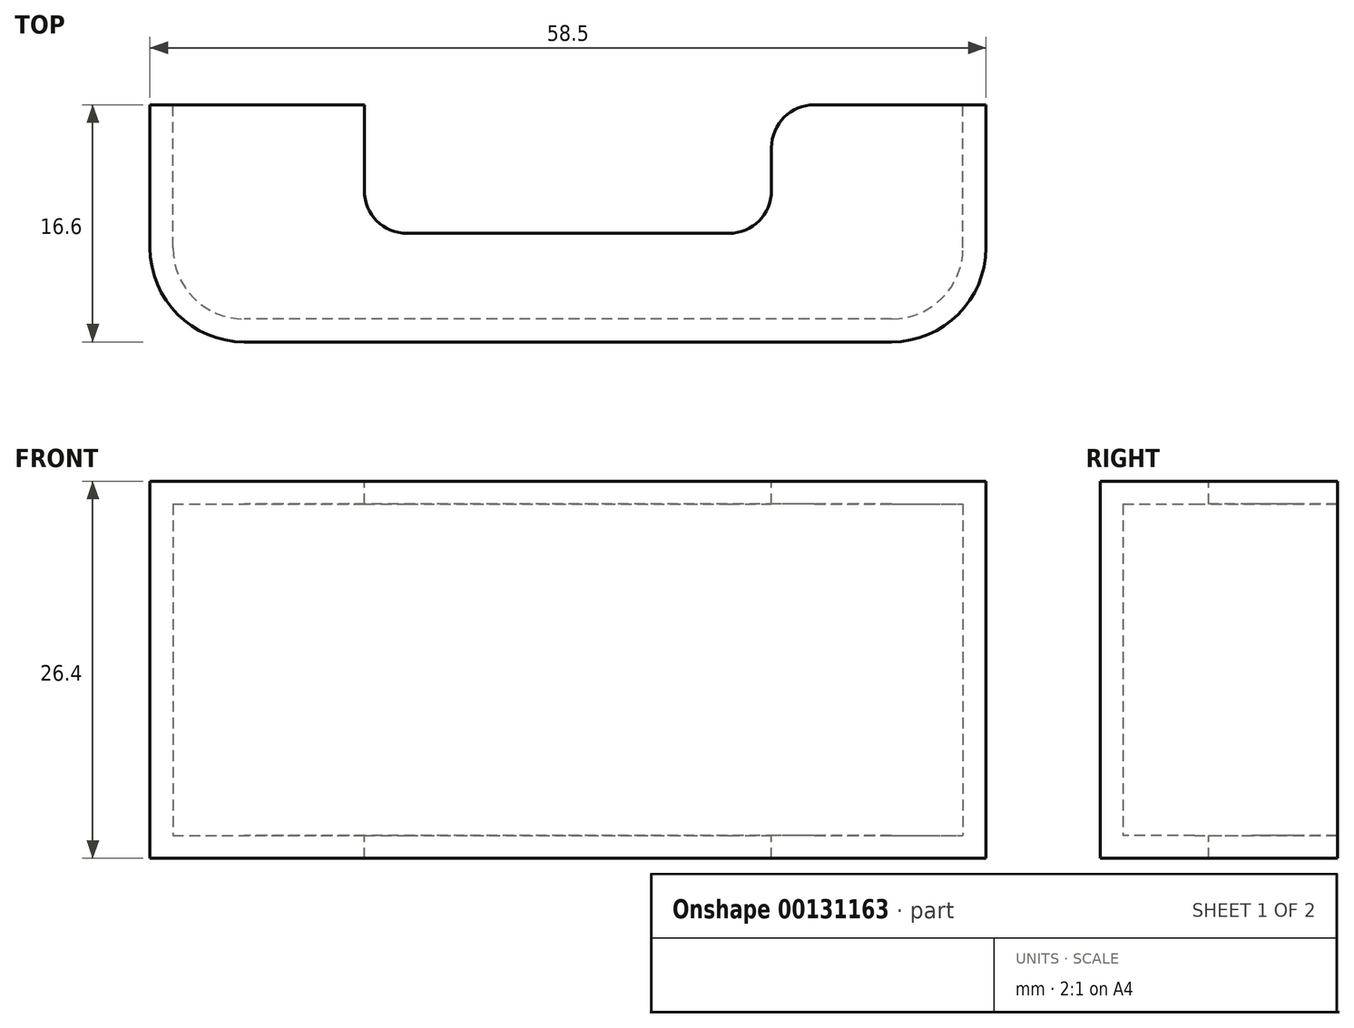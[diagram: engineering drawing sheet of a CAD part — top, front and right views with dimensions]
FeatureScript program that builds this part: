
annotation { "Feature Type Name" : "Feature", "Feature Type Description" : "" }
export const myFeature = defineFeature(function(context is Context, id is Id, definition is map)
    precondition{}
    {
        {
            var Q0;
            Q0=qCreatedBy(makeId("Top.planeOp"),FACE);
            var sketch = newSketch(context, id + "F0", { "sketchPlane" : qUnion([Q0])});
            skLineSegment(sketch, "E0.top", {"start": v(27.65, 7.5) * mm, "end": v(-27.65, 7.5) * mm});
            skPoint(sketch, "E0.middle", {"position": v(0, 0) * mm});
            skLineSegment(sketch, "E1.0", {"start": v(29.25, -9.1) * mm, "end": v(29.25, 7.5) * mm});
            skLineSegment(sketch, "E1.1", {"start": v(29.25, -9.1) * mm, "end": v(-29.25, -9.1) * mm});
            skLineSegment(sketch, "E1.2", {"start": v(-29.25, -9.1) * mm, "end": v(-29.25, 7.5) * mm});
            skPoint(sketch, "E0.bottom.end.orphan", {"position": v(-27.65, -7.5) * mm});
            skPoint(sketch, "E0.left.start.orphan", {"position": v(27.65, -7.5) * mm});
            skLineSegment(sketch, "E2", {"start": v(-29.25, 7.5) * mm, "end": v(-27.65, 7.5) * mm});
            skLineSegment(sketch, "E3", {"start": v(27.65, 7.5) * mm, "end": v(29.25, 7.5) * mm});
            skSolve(sketch);
        }
        {
            var Q0;
            Q0 = qSketchRegion(id + "F0", true);
            extrude(context, id + "F1", {"entities" : qUnion([Q0]), "depth" : 26.4 * mm});
        }
        {
            var Q0;
            Q0=makeQuery(id+"F1.opExtrude","SWEPT_EDGE",EDGE,{"disambiguationData":[OSD([sQuery(id+"F0.wireOp",EDGE,"E1.0"),sQuery(id+"F0.wireOp",EDGE,"E1.1")])]});
            var Q1;
            Q1=makeQuery(id+"F1.opExtrude","SWEPT_EDGE",EDGE,{"disambiguationData":[OSD([sQuery(id+"F0.wireOp",EDGE,"E1.1"),sQuery(id+"F0.wireOp",EDGE,"E1.2")])]});
            fillet(context, id + "F2", {"entities" : qUnion([Q0, Q1]), "radius" : 6.6 * mm, "tangentPropagation" : true, "allowEdgeOverflow" : false});
        }
        {
            var Q0;
            Q0=makeQuery(id+"F1.opExtrude","SWEPT_FACE",FACE,{"disambiguationData":[OSD([sQuery(id+"F0.wireOp",EDGE,"E0.top"),sQuery(id+"F0.wireOp",EDGE,"E2"),sQuery(id+"F0.wireOp",EDGE,"E3")])]});
            shell(context, id + "F3", {"entities" : qUnion([Q0]), "thickness" : 1.6 * mm});
        }
        {
            var Q0;
            Q0=makeQuery(id+"F1.opExtrude","CAP_FACE",FACE,{"disambiguationData":[OSD([sQuery(id+"F0.wireOp",EDGE,"E0.top"),sQuery(id+"F0.wireOp",EDGE,"E1.0"),sQuery(id+"F0.wireOp",EDGE,"E1.1"),sQuery(id+"F0.wireOp",EDGE,"E1.2"),sQuery(id+"F0.wireOp",EDGE,"E2"),sQuery(id+"F0.wireOp",EDGE,"E3")])],"isStart":false});
            var sketch = newSketch(context, id + "F4", { "sketchPlane" : qUnion([Q0])});
            skLineSegment(sketch, "E4", {"start": v(-14.25, 7.5) * mm, "end": v(-14.25, -60.34) * mm, "construction": true});
            skLineSegment(sketch, "E5", {"start": v(14.25, 7.5) * mm, "end": v(14.25, -22.1) * mm, "construction": true});
            skLineSegment(sketch, "E6", {"start": v(-31.93, -1.5) * mm, "end": v(33.13, -1.5) * mm, "construction": true});
            skLineSegment(sketch, "E7.bottom", {"start": v(-14.25, 7.5) * mm, "end": v(14.25, 7.5) * mm});
            skLineSegment(sketch, "E7.top", {"start": v(-14.25, -1.5) * mm, "end": v(14.25, -1.5) * mm});
            skLineSegment(sketch, "E7.left", {"start": v(-14.25, 7.5) * mm, "end": v(-14.25, -1.5) * mm});
            skLineSegment(sketch, "E7.right", {"start": v(14.25, 7.5) * mm, "end": v(14.25, -1.5) * mm});
            skSolve(sketch);
        }
        {
            var Q0;
            Q0=makeQuery(id+"F4.imprint","IMPRINT",FACE,{"disambiguationData":[TD([[makeQuery(id+"F4.imprint","IMPRINT",EDGE,{"derivedFrom":sQuery(id+"F4.wireOp",EDGE,"E7.bottom")}),-1.0]])]});
            extrude(context, id + "F5", {"entities" : qUnion([Q0]), "operationType" : NewBodyOperationType.REMOVE, "endBound" : BoundingType.THROUGH_ALL, "oppositeDirection" : true, "depth" : 25 * mm});
        }
        {
            var Q0;
            {var subQ0=sQuery(id+"F0.wireOp",EDGE,"E3");var subQ1=sQuery(id+"F0.wireOp",EDGE,"E2");var subQ2=sQuery(id+"F0.wireOp",EDGE,"E1.2");var subQ3=sQuery(id+"F0.wireOp",EDGE,"E1.1");var subQ4=sQuery(id+"F0.wireOp",EDGE,"E1.0");var subQ5=sQuery(id+"F0.wireOp",EDGE,"E0.top");var subQ6=makeQuery(id+"F1.opExtrude","CAP_FACE",FACE,{"disambiguationData":[OSD([subQ5,subQ4,subQ3,subQ2,subQ1,subQ0])],"isStart":false});var subQ7=sQuery(id+"F4.wireOp",EDGE,"E7.top");var subQ8=sQuery(id+"F4.wireOp",EDGE,"E7.right");Q0=makeQuery(id+"F5.boolean.opBoolean","COPY",EDGE,{"disambiguationData":[TD([subQ6])],"derivedFrom":makeQuery(id+"F5.opExtrude","SWEPT_EDGE",EDGE,{"disambiguationData":[OSD([subQ7,subQ8])]})});}
            var Q1;
            {var subQ0=sQuery(id+"F0.wireOp",EDGE,"E3");var subQ1=sQuery(id+"F0.wireOp",EDGE,"E2");var subQ2=sQuery(id+"F0.wireOp",EDGE,"E1.2");var subQ3=sQuery(id+"F0.wireOp",EDGE,"E1.1");var subQ4=sQuery(id+"F0.wireOp",EDGE,"E1.0");var subQ5=sQuery(id+"F0.wireOp",EDGE,"E0.top");var subQ6=makeQuery(id+"F1.opExtrude","CAP_FACE",FACE,{"disambiguationData":[OSD([subQ5,subQ4,subQ3,subQ2,subQ1,subQ0])],"isStart":false});var subQ7=sQuery(id+"F4.wireOp",EDGE,"E7.right");Q1=makeQuery(id+"F5.boolean.opBoolean","COPY",EDGE,{"disambiguationData":[TD([subQ6])],"derivedFrom":makeQuery(id+"F5.opExtrude","SWEPT_EDGE",EDGE,{"disambiguationData":[OSD([subQ5,subQ1,subQ0,sQuery(id+"F4.wireOp",EDGE,"E7.bottom"),subQ7])]})});}
            var Q2;
            {var subQ0=sQuery(id+"F0.wireOp",EDGE,"E3");var subQ1=sQuery(id+"F0.wireOp",EDGE,"E2");var subQ2=sQuery(id+"F0.wireOp",EDGE,"E1.2");var subQ3=sQuery(id+"F0.wireOp",EDGE,"E1.1");var subQ4=sQuery(id+"F0.wireOp",EDGE,"E1.0");var subQ5=sQuery(id+"F0.wireOp",EDGE,"E0.top");var subQ6=makeQuery(id+"F1.opExtrude","CAP_FACE",FACE,{"disambiguationData":[OSD([subQ5,subQ4,subQ3,subQ2,subQ1,subQ0])],"isStart":true});var subQ7=sQuery(id+"F4.wireOp",EDGE,"E7.right");Q2=makeQuery(id+"F5.boolean.opBoolean","COPY",EDGE,{"disambiguationData":[TD([subQ6])],"derivedFrom":makeQuery(id+"F5.opExtrude","SWEPT_EDGE",EDGE,{"disambiguationData":[OSD([subQ5,subQ1,subQ0,sQuery(id+"F4.wireOp",EDGE,"E7.bottom"),subQ7])]})});}
            var Q3;
            {var subQ0=sQuery(id+"F0.wireOp",EDGE,"E3");var subQ1=sQuery(id+"F0.wireOp",EDGE,"E2");var subQ2=sQuery(id+"F0.wireOp",EDGE,"E1.2");var subQ3=sQuery(id+"F0.wireOp",EDGE,"E1.1");var subQ4=sQuery(id+"F0.wireOp",EDGE,"E1.0");var subQ5=sQuery(id+"F0.wireOp",EDGE,"E0.top");var subQ6=makeQuery(id+"F1.opExtrude","CAP_FACE",FACE,{"disambiguationData":[OSD([subQ5,subQ4,subQ3,subQ2,subQ1,subQ0])],"isStart":true});var subQ7=sQuery(id+"F4.wireOp",EDGE,"E7.top");var subQ8=sQuery(id+"F4.wireOp",EDGE,"E7.right");Q3=makeQuery(id+"F5.boolean.opBoolean","COPY",EDGE,{"disambiguationData":[TD([subQ6])],"derivedFrom":makeQuery(id+"F5.opExtrude","SWEPT_EDGE",EDGE,{"disambiguationData":[OSD([subQ7,subQ8])]})});}
            var Q4;
            {var subQ0=sQuery(id+"F0.wireOp",EDGE,"E3");var subQ1=sQuery(id+"F0.wireOp",EDGE,"E2");var subQ2=sQuery(id+"F0.wireOp",EDGE,"E1.2");var subQ3=sQuery(id+"F0.wireOp",EDGE,"E1.1");var subQ4=sQuery(id+"F0.wireOp",EDGE,"E1.0");var subQ5=sQuery(id+"F0.wireOp",EDGE,"E0.top");var subQ6=makeQuery(id+"F1.opExtrude","CAP_FACE",FACE,{"disambiguationData":[OSD([subQ5,subQ4,subQ3,subQ2,subQ1,subQ0])],"isStart":false});var subQ7=sQuery(id+"F4.wireOp",EDGE,"E7.left");Q4=makeQuery(id+"F5.boolean.opBoolean","COPY",EDGE,{"disambiguationData":[TD([subQ6])],"derivedFrom":makeQuery(id+"F5.opExtrude","SWEPT_EDGE",EDGE,{"disambiguationData":[OSD([subQ5,subQ1,subQ0,sQuery(id+"F4.wireOp",EDGE,"E7.bottom"),subQ7])]})});}
            var Q5;
            {var subQ0=sQuery(id+"F0.wireOp",EDGE,"E3");var subQ1=sQuery(id+"F0.wireOp",EDGE,"E2");var subQ2=sQuery(id+"F0.wireOp",EDGE,"E1.2");var subQ3=sQuery(id+"F0.wireOp",EDGE,"E1.1");var subQ4=sQuery(id+"F0.wireOp",EDGE,"E1.0");var subQ5=sQuery(id+"F0.wireOp",EDGE,"E0.top");var subQ6=makeQuery(id+"F1.opExtrude","CAP_FACE",FACE,{"disambiguationData":[OSD([subQ5,subQ4,subQ3,subQ2,subQ1,subQ0])],"isStart":true});var subQ7=sQuery(id+"F4.wireOp",EDGE,"E7.left");Q5=makeQuery(id+"F5.boolean.opBoolean","COPY",EDGE,{"disambiguationData":[TD([subQ6])],"derivedFrom":makeQuery(id+"F5.opExtrude","SWEPT_EDGE",EDGE,{"disambiguationData":[OSD([subQ5,subQ1,subQ0,sQuery(id+"F4.wireOp",EDGE,"E7.bottom"),subQ7])]})});}
            var Q6;
            {var subQ0=sQuery(id+"F0.wireOp",EDGE,"E3");var subQ1=sQuery(id+"F0.wireOp",EDGE,"E2");var subQ2=sQuery(id+"F0.wireOp",EDGE,"E1.2");var subQ3=sQuery(id+"F0.wireOp",EDGE,"E1.1");var subQ4=sQuery(id+"F0.wireOp",EDGE,"E1.0");var subQ5=sQuery(id+"F0.wireOp",EDGE,"E0.top");var subQ6=makeQuery(id+"F1.opExtrude","CAP_FACE",FACE,{"disambiguationData":[OSD([subQ5,subQ4,subQ3,subQ2,subQ1,subQ0])],"isStart":true});var subQ7=sQuery(id+"F4.wireOp",EDGE,"E7.left");var subQ8=sQuery(id+"F4.wireOp",EDGE,"E7.top");Q6=makeQuery(id+"F5.boolean.opBoolean","COPY",EDGE,{"disambiguationData":[TD([subQ6])],"derivedFrom":makeQuery(id+"F5.opExtrude","SWEPT_EDGE",EDGE,{"disambiguationData":[OSD([subQ8,subQ7])]})});}
            var Q7;
            {var subQ0=sQuery(id+"F0.wireOp",EDGE,"E3");var subQ1=sQuery(id+"F0.wireOp",EDGE,"E2");var subQ2=sQuery(id+"F0.wireOp",EDGE,"E1.2");var subQ3=sQuery(id+"F0.wireOp",EDGE,"E1.1");var subQ4=sQuery(id+"F0.wireOp",EDGE,"E1.0");var subQ5=sQuery(id+"F0.wireOp",EDGE,"E0.top");var subQ6=makeQuery(id+"F1.opExtrude","CAP_FACE",FACE,{"disambiguationData":[OSD([subQ5,subQ4,subQ3,subQ2,subQ1,subQ0])],"isStart":false});var subQ7=sQuery(id+"F4.wireOp",EDGE,"E7.left");var subQ8=sQuery(id+"F4.wireOp",EDGE,"E7.top");Q7=makeQuery(id+"F5.boolean.opBoolean","COPY",EDGE,{"disambiguationData":[TD([subQ6])],"derivedFrom":makeQuery(id+"F5.opExtrude","SWEPT_EDGE",EDGE,{"disambiguationData":[OSD([subQ8,subQ7])]})});}
            fillet(context, id + "F6", {"entities" : qUnion([Q0, Q1, Q2, Q3, Q4, Q5, Q6, Q7]), "radius" : 3 * mm, "tangentPropagation" : true, "allowEdgeOverflow" : false});
        }
    });
